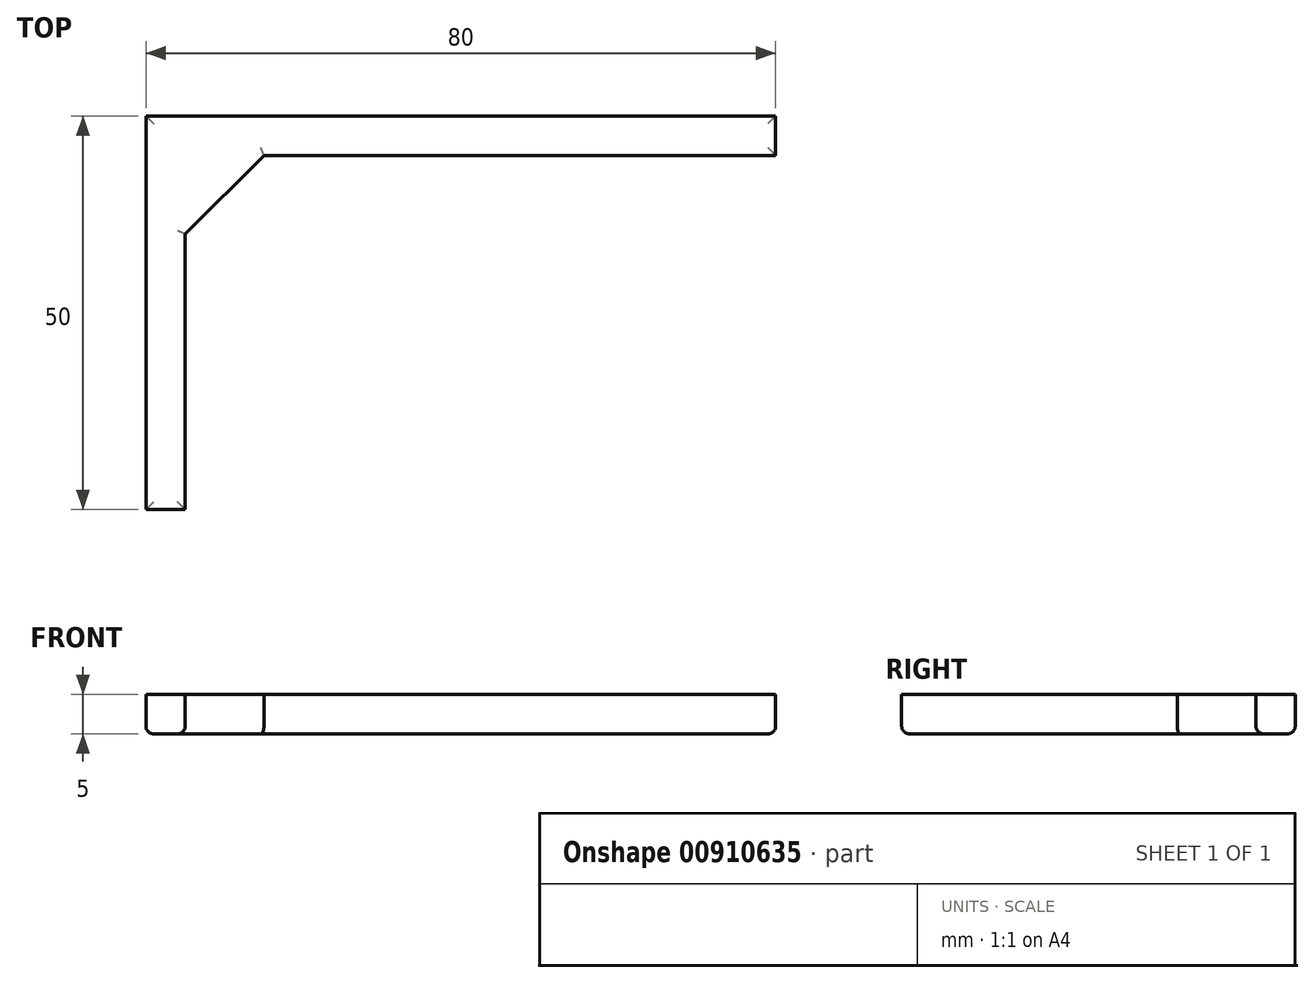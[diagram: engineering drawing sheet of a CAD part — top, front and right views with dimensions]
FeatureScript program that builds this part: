
annotation { "Feature Type Name" : "Feature", "Feature Type Description" : "" }
export const myFeature = defineFeature(function(context is Context, id is Id, definition is map)
    precondition{}
    {
        {
            var Q0;
            Q0=qCreatedBy(makeId("Top.planeOp"),FACE);
            var sketch = newSketch(context, id + "F0", { "sketchPlane" : qUnion([Q0])});
            skLineSegment(sketch, "E0.bottom", {"start": v(0, 0) * mm, "end": v(80, 0) * mm});
            skLineSegment(sketch, "E0.top", {"start": v(0, -50) * mm, "end": v(5, -50) * mm});
            skLineSegment(sketch, "E0.left", {"start": v(0, 0) * mm, "end": v(0, -50) * mm});
            skLineSegment(sketch, "E0.right", {"start": v(80, 0) * mm, "end": v(80, -5) * mm});
            skLineSegment(sketch, "E1.bottom", {"start": v(0, 0) * mm, "end": v(5, 0) * mm, "construction": true});
            skLineSegment(sketch, "E1.left", {"start": v(0, 0) * mm, "end": v(0, -5) * mm, "construction": true});
            skLineSegment(sketch, "E2.bottom", {"start": v(15, -5) * mm, "end": v(80, -5) * mm});
            skLineSegment(sketch, "E2.left", {"start": v(5, -15) * mm, "end": v(5, -50) * mm});
            skLineSegment(sketch, "E3.bottom", {"start": v(0, 0) * mm, "end": v(15, 0) * mm, "construction": true});
            skLineSegment(sketch, "E3.top", {"start": v(0, -15) * mm, "end": v(15, -15) * mm, "construction": true});
            skLineSegment(sketch, "E3.left", {"start": v(0, 0) * mm, "end": v(0, -15) * mm, "construction": true});
            skLineSegment(sketch, "E3.right", {"start": v(15, 0) * mm, "end": v(15, -15) * mm, "construction": true});
            skLineSegment(sketch, "E4", {"start": v(15, -5) * mm, "end": v(5, -15) * mm});
            skSolve(sketch);
        }
        {
            var Q0;
            Q0 = qSketchRegion(id + "F0", true);
            extrude(context, id + "F1", {"entities" : qUnion([Q0]), "depth" : 5 * mm, "offsetDistance" : 25 * mm});
        }
        {
            var Q0;
            Q0=makeQuery(id+"F1.opExtrude","CAP_EDGE",EDGE,{"disambiguationData":[OSD([sQuery(id+"F0.wireOp",EDGE,"E0.bottom")])],"isStart":true});
            var Q1;
            Q1=makeQuery(id+"F1.opExtrude","CAP_EDGE",EDGE,{"disambiguationData":[OSD([sQuery(id+"F0.wireOp",EDGE,"E0.left")])],"isStart":true});
            var Q2;
            Q2=makeQuery(id+"F1.opExtrude","CAP_EDGE",EDGE,{"disambiguationData":[OSD([sQuery(id+"F0.wireOp",EDGE,"E0.right")])],"isStart":true});
            var Q3;
            Q3=makeQuery(id+"F1.opExtrude","CAP_EDGE",EDGE,{"disambiguationData":[OSD([sQuery(id+"F0.wireOp",EDGE,"E2.bottom")])],"isStart":true});
            var Q4;
            Q4=makeQuery(id+"F1.opExtrude","CAP_EDGE",EDGE,{"disambiguationData":[OSD([sQuery(id+"F0.wireOp",EDGE,"E4")])],"isStart":true});
            var Q5;
            Q5=makeQuery(id+"F1.opExtrude","CAP_EDGE",EDGE,{"disambiguationData":[OSD([sQuery(id+"F0.wireOp",EDGE,"E2.left")])],"isStart":true});
            var Q6;
            Q6=makeQuery(id+"F1.opExtrude","CAP_EDGE",EDGE,{"disambiguationData":[OSD([sQuery(id+"F0.wireOp",EDGE,"E0.top")])],"isStart":true});
            fillet(context, id + "F2", {"entities" : qUnion([Q0, Q1, Q2, Q3, Q4, Q5, Q6]), "radius" : 1 * mm, "tangentPropagation" : true, "allowEdgeOverflow" : false});
        }
    });
